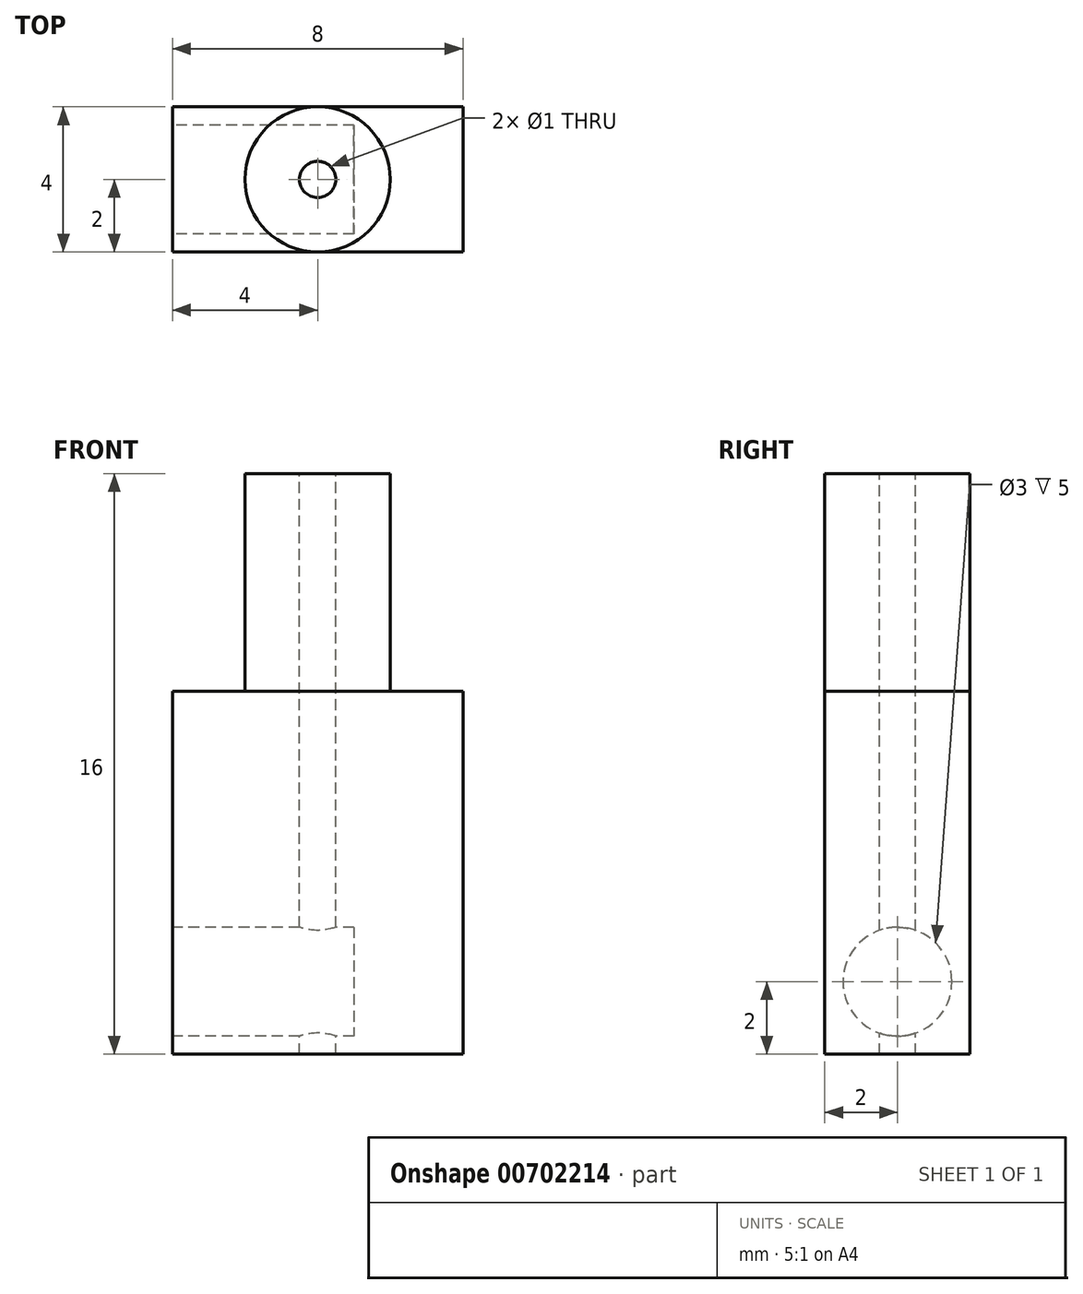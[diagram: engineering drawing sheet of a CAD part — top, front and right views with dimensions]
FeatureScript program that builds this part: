
annotation { "Feature Type Name" : "Feature", "Feature Type Description" : "" }
export const myFeature = defineFeature(function(context is Context, id is Id, definition is map)
    precondition{}
    {
        {
            var Q0;
            Q0=qCreatedBy(makeId("Right.planeOp"),FACE);
            var sketch = newSketch(context, id + "F0", { "sketchPlane" : qUnion([Q0])});
            skLineSegment(sketch, "E0.bottom", {"start": v(-2, 5) * mm, "end": v(2, 5) * mm});
            skLineSegment(sketch, "E0.top", {"start": v(-2, -5) * mm, "end": v(2, -5) * mm});
            skLineSegment(sketch, "E0.left", {"start": v(-2, 5) * mm, "end": v(-2, -5) * mm});
            skLineSegment(sketch, "E0.right", {"start": v(2, 5) * mm, "end": v(2, -5) * mm});
            skPoint(sketch, "E0.middle", {"position": v(0, 0) * mm});
            skSolve(sketch);
        }
        {
            var Q0;
            Q0=makeQuery(id+"F0.imprint","IMPRINT",FACE,{"disambiguationData":[TD([[makeQuery(id+"F0.imprint","IMPRINT",EDGE,{"derivedFrom":sQuery(id+"F0.wireOp",EDGE,"E0.bottom")}),-1.0]])]});
            extrude(context, id + "F1", {"entities" : qUnion([Q0]), "depth" : 8 * mm, "offsetDistance" : 25 * mm});
        }
        {
            var Q0;
            Q0=makeQuery(id+"F1.opExtrude","CAP_FACE",FACE,{"disambiguationData":[OSD([sQuery(id+"F0.wireOp",EDGE,"E0.bottom"),sQuery(id+"F0.wireOp",EDGE,"E0.top"),sQuery(id+"F0.wireOp",EDGE,"E0.left"),sQuery(id+"F0.wireOp",EDGE,"E0.right")])],"isStart":true});
            var sketch = newSketch(context, id + "F2", { "sketchPlane" : qUnion([Q0])});
            skPoint(sketch, "E1", {"position": v(0, -3) * mm});
            skCircle(sketch, "E2", {"center": v(0, -3) * mm, "radius": 1.5 * mm});
            skSolve(sketch);
        }
        {
            var Q0;
            Q0=makeQuery(id+"F2.imprint","IMPRINT",FACE,{"disambiguationData":[TD([[makeQuery(id+"F2.imprint","IMPRINT",EDGE,{"derivedFrom":sQuery(id+"F2.wireOp",EDGE,"E2")}),1.0]])]});
            extrude(context, id + "F3", {"entities" : qUnion([Q0]), "operationType" : NewBodyOperationType.REMOVE, "oppositeDirection" : true, "depth" : 5 * mm, "offsetDistance" : 25 * mm});
        }
        {
            var Q0;
            Q0=makeQuery(id+"F1.opExtrude","SWEPT_FACE",FACE,{"disambiguationData":[OSD([sQuery(id+"F0.wireOp",EDGE,"E0.bottom")])]});
            var sketch = newSketch(context, id + "F4", { "sketchPlane" : qUnion([Q0])});
            skPoint(sketch, "E3", {"position": v(4, 0) * mm});
            skCircle(sketch, "E4", {"center": v(4, 0) * mm, "radius": 2 * mm});
            skSolve(sketch);
        }
        {
            var Q0;
            {var subQ0=sQuery(id+"F4.wireOp",EDGE,"E4");var subQ1=sQuery(id+"F0.wireOp",EDGE,"E0.bottom");var subQ2=makeQuery(id+"F4.imprint","INTERSECT",VERTEX,{"derivedFrom":[makeQuery(id+"F1.opExtrude","SWEPT_EDGE",EDGE,{"disambiguationData":[OSD([subQ1,sQuery(id+"F0.wireOp",EDGE,"E0.left")])]}),subQ0]});Q0=makeQuery(id+"F4.imprint","IMPRINT",FACE,{"disambiguationData":[TD([[makeQuery(id+"F4.imprint","IMPRINT",EDGE,{"disambiguationData":[TD([[subQ2,1.0]])],"derivedFrom":subQ0}),1.0]])]});}
            extrude(context, id + "F5", {"entities" : qUnion([Q0]), "operationType" : NewBodyOperationType.ADD, "depth" : 6 * mm, "offsetDistance" : 25 * mm});
        }
        {
            var Q0;
            Q0=makeQuery(id+"F5.opExtrude","CAP_FACE",FACE,{"disambiguationData":[OSD([sQuery(id+"F4.wireOp",EDGE,"E4")])],"isStart":false});
            var sketch = newSketch(context, id + "F6", { "sketchPlane" : qUnion([Q0])});
            skPoint(sketch, "E5", {"position": v(4, 0) * mm});
            skSolve(sketch);
        }
        {
            var Q0;
            Q0=sQuery(id+"F6.wireOp",VERTEX,"E5");
            var Q1;
            Q1=makeQuery(id+"F1.opExtrude","SWEPT_BODY",BODY,{"disambiguationData":[OSD([sQuery(id+"F0.wireOp",EDGE,"E0.bottom"),sQuery(id+"F0.wireOp",EDGE,"E0.top"),sQuery(id+"F0.wireOp",EDGE,"E0.left"),sQuery(id+"F0.wireOp",EDGE,"E0.right")])]});
            hole(context, id + "F7", {"style" : HoleStyle.SIMPLE, "endStyle" : HoleEndStyle.THROUGH, "holeDiameter" : 1 * mm, "majorDiameter" : 5 * mm, "isTappedThrough" : true, "tappedDepth" : 4 * mm, "tapClearance" : 4, "locations" : qUnion([Q0]), "scope" : qUnion([Q1])});
        }
    });
